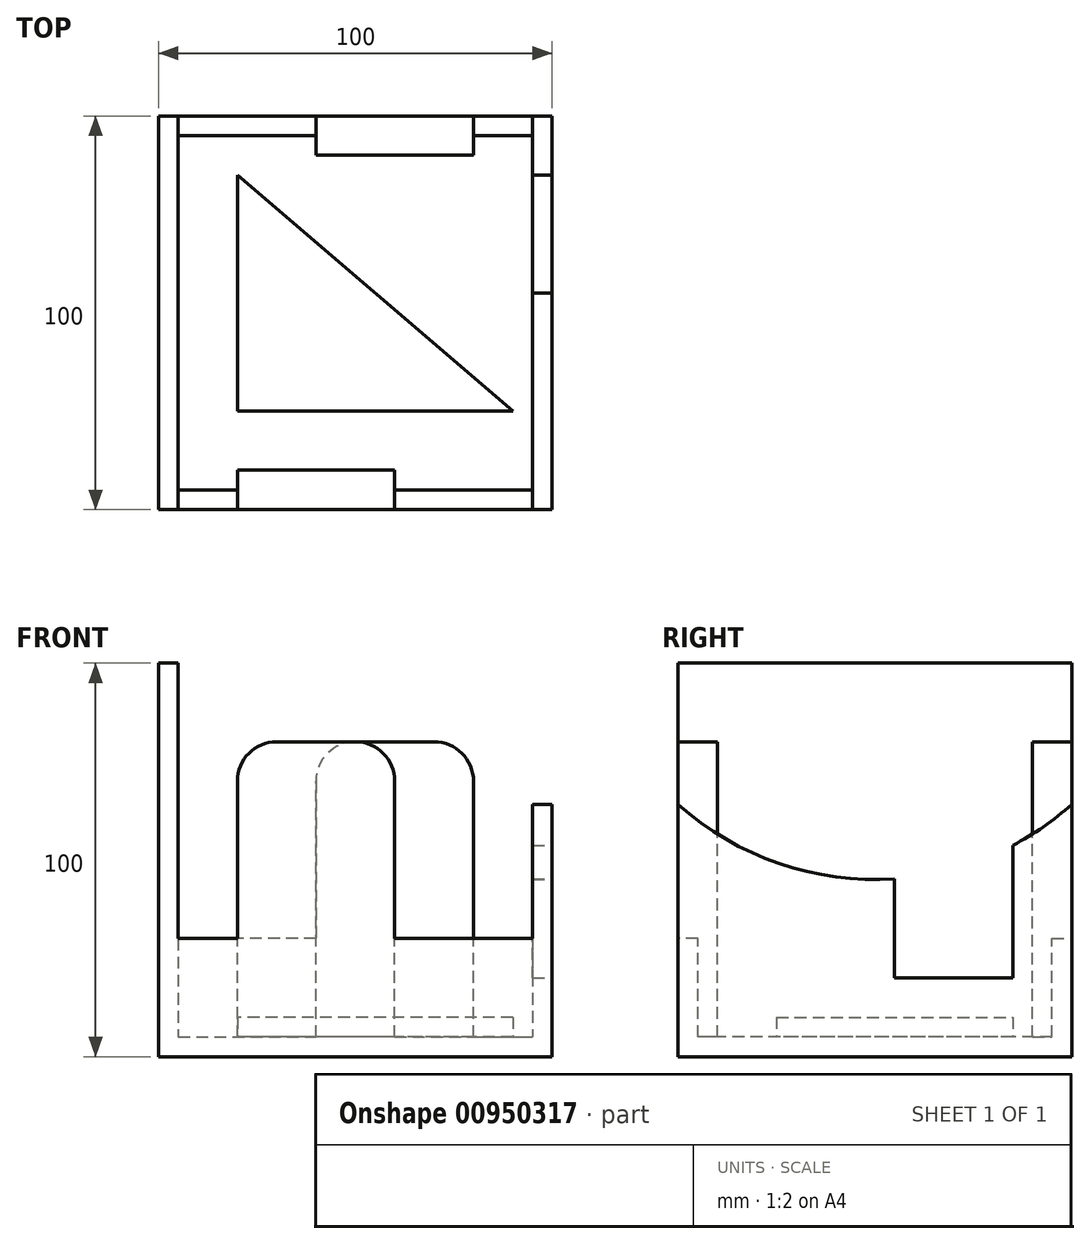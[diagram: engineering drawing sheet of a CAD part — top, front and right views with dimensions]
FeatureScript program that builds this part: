
annotation { "Feature Type Name" : "Feature", "Feature Type Description" : "" }
export const myFeature = defineFeature(function(context is Context, id is Id, definition is map)
    precondition{}
    {
        {
            var Q0;
            Q0=qCreatedBy(makeId("Top.planeOp"),FACE);
            var sketch = newSketch(context, id + "F0", { "sketchPlane" : qUnion([Q0])});
            skLineSegment(sketch, "E0.bottom", {"start": v(0, 0) * mm, "end": v(100, 0) * mm});
            skLineSegment(sketch, "E0.top", {"start": v(0, 100) * mm, "end": v(100, 100) * mm});
            skLineSegment(sketch, "E0.left", {"start": v(0, 0) * mm, "end": v(0, 100) * mm});
            skLineSegment(sketch, "E0.right", {"start": v(100, 0) * mm, "end": v(100, 100) * mm});
            skSolve(sketch);
        }
        {
            var Q0;
            Q0 = qSketchRegion(id + "F0", true);
            extrude(context, id + "F1", {"entities" : qUnion([Q0]), "depth" : 5 * mm, "offsetDistance" : 25 * mm});
        }
        {
            var Q0;
            Q0=makeQuery(id+"F1.opExtrude","CAP_FACE",FACE,{"disambiguationData":[OSD([sQuery(id+"F0.wireOp",EDGE,"E0.bottom"),sQuery(id+"F0.wireOp",EDGE,"E0.top"),sQuery(id+"F0.wireOp",EDGE,"E0.left"),sQuery(id+"F0.wireOp",EDGE,"E0.right")])],"isStart":false});
            var sketch = newSketch(context, id + "F2", { "sketchPlane" : qUnion([Q0])});
            skLineSegment(sketch, "E1.bottom", {"start": v(0, 100) * mm, "end": v(5, 100) * mm});
            skLineSegment(sketch, "E1.top", {"start": v(0, 0) * mm, "end": v(5, 0) * mm});
            skLineSegment(sketch, "E1.left", {"start": v(0, 100) * mm, "end": v(0, 0) * mm});
            skLineSegment(sketch, "E1.right", {"start": v(5, 100) * mm, "end": v(5, 0) * mm});
            skSolve(sketch);
        }
        {
            var Q0;
            Q0 = qSketchRegion(id + "F2", true);
            extrude(context, id + "F3", {"entities" : qUnion([Q0]), "operationType" : NewBodyOperationType.ADD, "depth" : 95 * mm, "offsetDistance" : 25 * mm});
        }
        {
            var Q0;
            Q0=makeQuery(id+"F1.opExtrude","CAP_FACE",FACE,{"disambiguationData":[OSD([sQuery(id+"F0.wireOp",EDGE,"E0.bottom"),sQuery(id+"F0.wireOp",EDGE,"E0.top"),sQuery(id+"F0.wireOp",EDGE,"E0.left"),sQuery(id+"F0.wireOp",EDGE,"E0.right")])],"isStart":false});
            var sketch = newSketch(context, id + "F4", { "sketchPlane" : qUnion([Q0])});
            skLineSegment(sketch, "E2", {"start": v(20, 85) * mm, "end": v(20, 25) * mm});
            skLineSegment(sketch, "E3", {"start": v(20, 25) * mm, "end": v(90, 25) * mm});
            skLineSegment(sketch, "E4", {"start": v(90, 25) * mm, "end": v(20, 85) * mm});
            skSolve(sketch);
        }
        {
            var Q0;
            Q0 = qSketchRegion(id + "F4", true);
            extrude(context, id + "F5", {"entities" : qUnion([Q0]), "operationType" : NewBodyOperationType.ADD, "depth" : 5 * mm, "offsetDistance" : 25 * mm});
        }
        {
            var Q0;
            Q0=makeQuery(id+"F1.opExtrude","SWEPT_FACE",FACE,{"disambiguationData":[OSD([sQuery(id+"F0.wireOp",EDGE,"E0.right")])]});
            var sketch = newSketch(context, id + "F6", { "sketchPlane" : qUnion([Q0])});
            skLineSegment(sketch, "E5", {"start": v(0, 5) * mm, "end": v(0, 64.1) * mm});
            skLineSegment(sketch, "E6", {"start": v(100, 64.1) * mm, "end": v(100, 5) * mm});
            skLineSegment(sketch, "E7", {"start": v(100, 5) * mm, "end": v(0, 5) * mm});
            skArc(sketch, "E8", {"start": v(0, 64.1) * mm, "mid": v(25.59, 49.08) * mm, "end": v(55, 45.17) * mm});
            skLineSegment(sketch, "E9", {"start": v(55, 45.17) * mm, "end": v(55, 20) * mm});
            skLineSegment(sketch, "E10", {"start": v(55, 20) * mm, "end": v(85, 20) * mm});
            skLineSegment(sketch, "E11", {"start": v(85, 20) * mm, "end": v(85, 53.67) * mm});
            skArc(sketch, "E12.trimOffspring", {"start": v(85, 53.67) * mm, "mid": v(92.82, 58.42) * mm, "end": v(100, 64.1) * mm});
            skSolve(sketch);
        }
        {
            var Q0;
            Q0 = qSketchRegion(id + "F6", true);
            extrude(context, id + "F7", {"entities" : qUnion([Q0]), "operationType" : NewBodyOperationType.ADD, "oppositeDirection" : true, "depth" : 5 * mm, "offsetDistance" : 25 * mm});
        }
        {
            var Q0;
            Q0=makeQuery(id+"F7.boolean.opBoolean","MERGE",FACE,{"derivedFrom":[makeQuery(id+"F3.boolean.opBoolean","MERGE",FACE,{"derivedFrom":[makeQuery(id+"F1.opExtrude","SWEPT_FACE",FACE,{"disambiguationData":[OSD([sQuery(id+"F0.wireOp",EDGE,"E0.bottom")])]}),makeQuery(id+"F3.opExtrude","SWEPT_FACE",FACE,{"disambiguationData":[OSD([sQuery(id+"F2.wireOp",EDGE,"E1.top")])]})]}),makeQuery(id+"F7.opExtrude","SWEPT_FACE",FACE,{"disambiguationData":[OSD([sQuery(id+"F6.wireOp",EDGE,"E5")])]})]});
            var sketch = newSketch(context, id + "F8", { "sketchPlane" : qUnion([Q0])});
            skLineSegment(sketch, "E13", {"start": v(5, 5) * mm, "end": v(5, 30) * mm});
            skLineSegment(sketch, "E14", {"start": v(5, 30) * mm, "end": v(20, 30) * mm});
            skLineSegment(sketch, "E15", {"start": v(20, 30) * mm, "end": v(20, 80) * mm});
            skLineSegment(sketch, "E16", {"start": v(20, 80) * mm, "end": v(60, 80) * mm});
            skLineSegment(sketch, "E17", {"start": v(60, 80) * mm, "end": v(60, 30) * mm});
            skLineSegment(sketch, "E18", {"start": v(60, 30) * mm, "end": v(95, 30) * mm});
            skLineSegment(sketch, "E19", {"start": v(95, 30) * mm, "end": v(95, 5) * mm});
            skLineSegment(sketch, "E20", {"start": v(95, 5) * mm, "end": v(5, 5) * mm});
            skSolve(sketch);
        }
        {
            var Q0;
            Q0 = qSketchRegion(id + "F8", true);
            extrude(context, id + "F9", {"entities" : qUnion([Q0]), "operationType" : NewBodyOperationType.ADD, "oppositeDirection" : true, "depth" : 5 * mm, "offsetDistance" : 25 * mm});
        }
        {
            var Q0;
            Q0=makeQuery(id+"F7.boolean.opBoolean","MERGE",FACE,{"derivedFrom":[makeQuery(id+"F3.boolean.opBoolean","MERGE",FACE,{"derivedFrom":[makeQuery(id+"F1.opExtrude","SWEPT_FACE",FACE,{"disambiguationData":[OSD([sQuery(id+"F0.wireOp",EDGE,"E0.top")])]}),makeQuery(id+"F3.opExtrude","SWEPT_FACE",FACE,{"disambiguationData":[OSD([sQuery(id+"F2.wireOp",EDGE,"E1.bottom")])]})]}),makeQuery(id+"F7.opExtrude","SWEPT_FACE",FACE,{"disambiguationData":[OSD([sQuery(id+"F6.wireOp",EDGE,"E6")])]})]});
            var sketch = newSketch(context, id + "F10", { "sketchPlane" : qUnion([Q0])});
            skLineSegment(sketch, "E21", {"start": v(-5, 5) * mm, "end": v(-95, 5) * mm});
            skLineSegment(sketch, "E22", {"start": v(-95, 5) * mm, "end": v(-95, 30) * mm});
            skLineSegment(sketch, "E23", {"start": v(-95, 30) * mm, "end": v(-80, 30) * mm});
            skLineSegment(sketch, "E24", {"start": v(-80, 30) * mm, "end": v(-80, 80) * mm});
            skLineSegment(sketch, "E25", {"start": v(-80, 80) * mm, "end": v(-40, 80) * mm});
            skLineSegment(sketch, "E26", {"start": v(-40, 80) * mm, "end": v(-40, 30) * mm});
            skLineSegment(sketch, "E27", {"start": v(-40, 30) * mm, "end": v(-5, 30) * mm});
            skLineSegment(sketch, "E28", {"start": v(-5, 30) * mm, "end": v(-5, 5) * mm});
            skSolve(sketch);
        }
        {
            var Q0;
            Q0 = qSketchRegion(id + "F10", true);
            extrude(context, id + "F11", {"entities" : qUnion([Q0]), "operationType" : NewBodyOperationType.ADD, "oppositeDirection" : true, "depth" : 5 * mm, "offsetDistance" : 25 * mm});
        }
        {
            var Q0;
            Q0=makeQuery(id+"F9.opExtrude","SWEPT_FACE",FACE,{"disambiguationData":[OSD([sQuery(id+"F8.wireOp",EDGE,"E16")])]});
            var sketch = newSketch(context, id + "F12", { "sketchPlane" : qUnion([Q0])});
            skLineSegment(sketch, "E29.bottom", {"start": v(20, 5) * mm, "end": v(60, 5) * mm});
            skLineSegment(sketch, "E29.top", {"start": v(20, 10) * mm, "end": v(60, 10) * mm});
            skLineSegment(sketch, "E29.left", {"start": v(20, 5) * mm, "end": v(20, 10) * mm});
            skLineSegment(sketch, "E29.right", {"start": v(60, 5) * mm, "end": v(60, 10) * mm});
            skSolve(sketch);
        }
        {
            var Q0;
            Q0 = qSketchRegion(id + "F12", true);
            extrude(context, id + "F13", {"entities" : qUnion([Q0]), "operationType" : NewBodyOperationType.ADD, "endBound" : BoundingType.UP_TO_NEXT, "oppositeDirection" : true, "depth" : 25 * mm, "offsetDistance" : 25 * mm});
        }
        {
            var Q0;
            Q0=makeQuery(id+"F11.opExtrude","SWEPT_FACE",FACE,{"disambiguationData":[OSD([sQuery(id+"F10.wireOp",EDGE,"E25")])]});
            var sketch = newSketch(context, id + "F14", { "sketchPlane" : qUnion([Q0])});
            skLineSegment(sketch, "E30.bottom", {"start": v(40, 95) * mm, "end": v(80, 95) * mm});
            skLineSegment(sketch, "E30.top", {"start": v(40, 90) * mm, "end": v(80, 90) * mm});
            skLineSegment(sketch, "E30.left", {"start": v(40, 95) * mm, "end": v(40, 90) * mm});
            skLineSegment(sketch, "E30.right", {"start": v(80, 95) * mm, "end": v(80, 90) * mm});
            skSolve(sketch);
        }
        {
            var Q0;
            Q0 = qSketchRegion(id + "F14", true);
            extrude(context, id + "F15", {"entities" : qUnion([Q0]), "operationType" : NewBodyOperationType.ADD, "endBound" : BoundingType.UP_TO_NEXT, "oppositeDirection" : true, "depth" : 25 * mm, "offsetDistance" : 25 * mm});
        }
        {
            var Q0;
            Q0=makeQuery(id+"F13.boolean.opBoolean","MERGE",EDGE,{"derivedFrom":[makeQuery(id+"F9.opExtrude","SWEPT_EDGE",EDGE,{"disambiguationData":[OSD([sQuery(id+"F8.wireOp",EDGE,"E16"),sQuery(id+"F8.wireOp",EDGE,"E17")])]}),makeQuery(id+"F13.opExtrude","CAP_EDGE",EDGE,{"disambiguationData":[OSD([sQuery(id+"F12.wireOp",EDGE,"E29.right")])],"isStart":true})]});
            var Q1;
            Q1=makeQuery(id+"F13.boolean.opBoolean","MERGE",EDGE,{"derivedFrom":[makeQuery(id+"F9.opExtrude","SWEPT_EDGE",EDGE,{"disambiguationData":[OSD([sQuery(id+"F8.wireOp",EDGE,"E15"),sQuery(id+"F8.wireOp",EDGE,"E16")])]}),makeQuery(id+"F13.opExtrude","CAP_EDGE",EDGE,{"disambiguationData":[OSD([sQuery(id+"F12.wireOp",EDGE,"E29.left")])],"isStart":true})]});
            var Q2;
            Q2=makeQuery(id+"F15.boolean.opBoolean","MERGE",EDGE,{"derivedFrom":[makeQuery(id+"F11.opExtrude","SWEPT_EDGE",EDGE,{"disambiguationData":[OSD([sQuery(id+"F10.wireOp",EDGE,"E24"),sQuery(id+"F10.wireOp",EDGE,"E25")])]}),makeQuery(id+"F15.opExtrude","CAP_EDGE",EDGE,{"disambiguationData":[OSD([sQuery(id+"F14.wireOp",EDGE,"E30.right")])],"isStart":true})]});
            var Q3;
            Q3=makeQuery(id+"F15.boolean.opBoolean","MERGE",EDGE,{"derivedFrom":[makeQuery(id+"F11.opExtrude","SWEPT_EDGE",EDGE,{"disambiguationData":[OSD([sQuery(id+"F10.wireOp",EDGE,"E25"),sQuery(id+"F10.wireOp",EDGE,"E26")])]}),makeQuery(id+"F15.opExtrude","CAP_EDGE",EDGE,{"disambiguationData":[OSD([sQuery(id+"F14.wireOp",EDGE,"E30.left")])],"isStart":true})]});
            fillet(context, id + "F16", {"entities" : qUnion([Q0, Q1, Q2, Q3]), "radius" : 10 * mm, "tangentPropagation" : true, "allowEdgeOverflow" : false});
        }
    });
